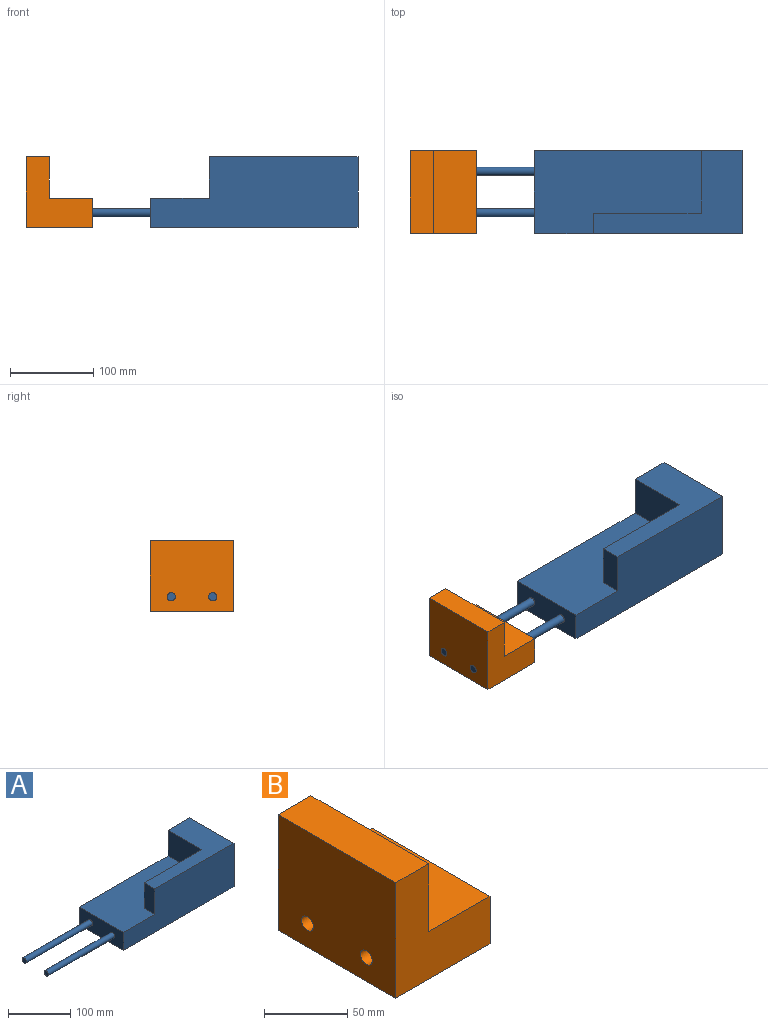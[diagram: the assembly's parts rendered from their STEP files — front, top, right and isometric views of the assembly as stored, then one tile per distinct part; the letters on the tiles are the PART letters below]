
ASSEMBLY  parts=2 mates=1
PART A: 14 faces, bbox 400x100x85 mm
  f0: plane 250x100mm, normal (0,0,-1), area 25000mm2, adj f1,f3,f4,f5
  f1: plane 100x85mm, normal (1,0,0), area 8500mm2, adj f0,f4,f5,f9
  f2: plane 200.7x100mm, normal (0,0,1), area 16897.8mm2, adj f3,f4,f5,f6,f7,f8
  f3: plane 100x35mm, normal (-1,0,0), area 3342.9mm2, adj f0,f2,f4,f5,f10,f12
  f4: plane 250x85mm, normal (0,-1,0), area 17699.8mm2, adj f0,f1,f2,f3,f8,f9
  f5: plane 250x85mm, normal (0,1,0), area 11214.9mm2, adj f0,f1,f2,f3,f6,f9
  f6: plane 75.54x50mm, normal (-1,0,0), area 3777mm2, adj f2,f5,f7,f9
  f7: plane 129.7x50mm, normal (0,1,0), area 6484.9mm2, adj f2,f6,f8,f9
  f8: plane 50x24.46mm, normal (-1,0,0), area 1223mm2, adj f2,f4,f7,f9
  f9: plane 179x100mm, normal (0,0,1), area 8102.2mm2, adj f1,f4,f5,f6,f7,f8
  f10: cylinder r=5mm len=150mm, axis (1,0,0), area 4712.4mm2, adj f3,f11
  f11: plane 10x10mm, normal (-1,0,0), area 78.5mm2, adj f10
  f12: cylinder r=5mm len=150mm, axis (1,0,0), area 4712.4mm2, adj f3,f13
  f13: plane 10x10mm, normal (-1,0,0), area 78.5mm2, adj f12
PART B: 10 faces, bbox 80x100x85 mm
  f0: plane 100x85mm, normal (-1,0,0), area 8342.9mm2, adj f2,f3,f5,f7,f8,f9
  f1: plane 100x35mm, normal (1,0,0), area 3342.9mm2, adj f2,f3,f4,f5,f8,f9
  f2: plane 100x80mm, normal (0,0,-1), area 8000mm2, adj f0,f1,f3,f5
  f3: plane 85x80mm, normal (0,1,0), area 4198.9mm2, adj f0,f1,f2,f4,f6,f7
  f4: plane 100x52.02mm, normal (0,0,1), area 5202.1mm2, adj f1,f3,f5,f6
  f5: plane 85x80mm, normal (0,-1,0), area 4198.9mm2, adj f0,f1,f2,f4,f6,f7
  f6: plane 100x50mm, normal (1,0,0), area 5000mm2, adj f3,f4,f5,f7
  f7: plane 100x27.98mm, normal (0,0,1), area 2797.9mm2, adj f0,f3,f5,f6
  f8: cylinder r=5mm len=80mm, axis (1,0,0), area 2513.3mm2, adj f0,f1
  f9: cylinder r=5mm len=80mm, axis (1,0,0), area 2513.3mm2, adj f0,f1
PLACE A at identity fixed
PLACE B t=(-195,0,0)mm
MATE slider B.f9 <-> A.f12  axis (-1,0,0) through (-275,-25,0)mm
